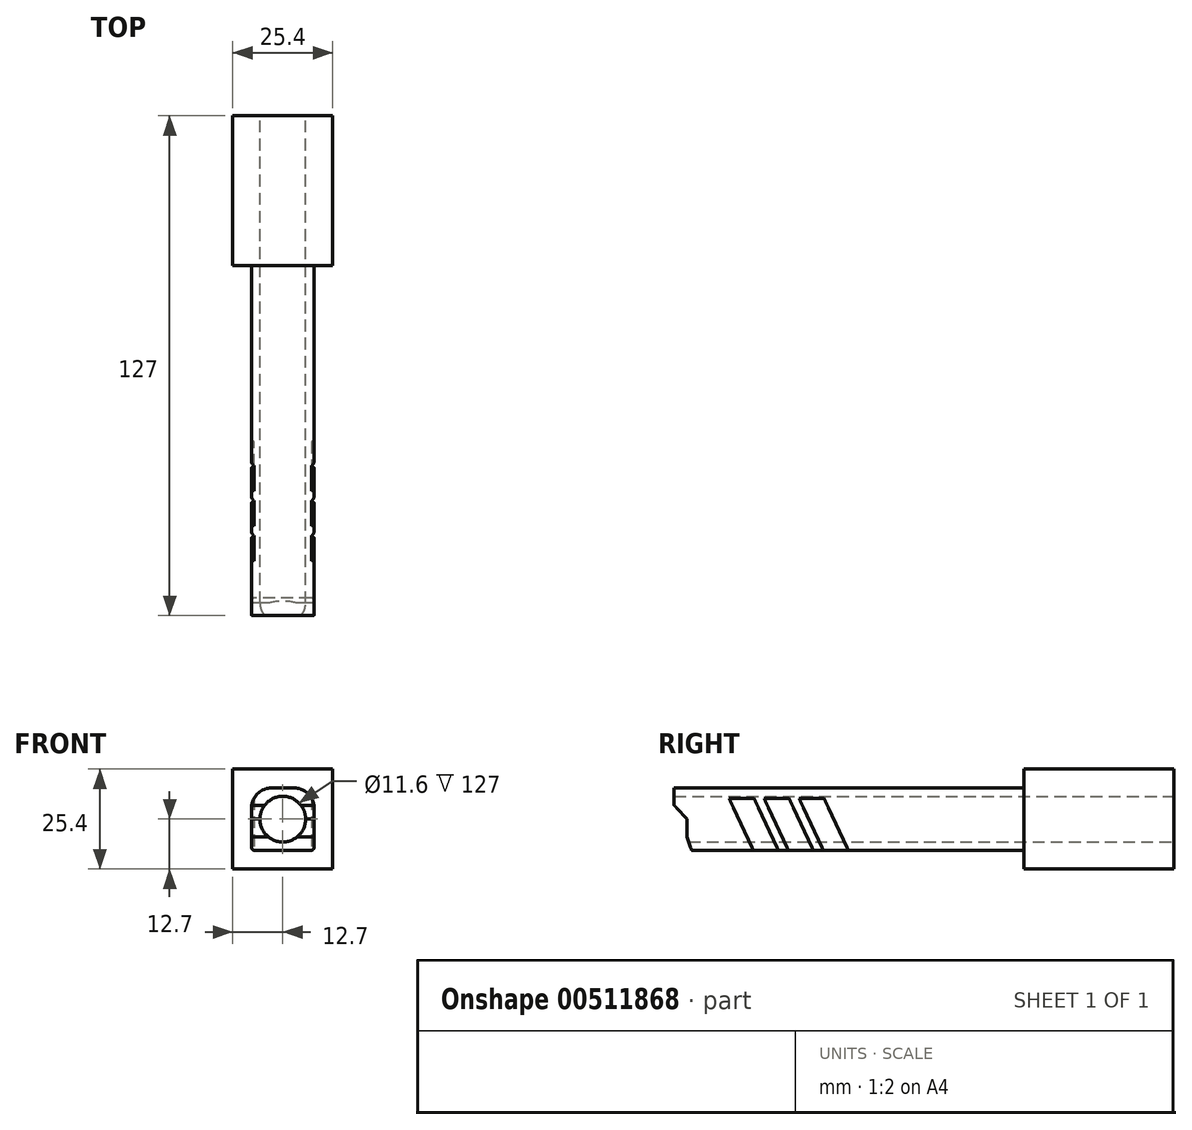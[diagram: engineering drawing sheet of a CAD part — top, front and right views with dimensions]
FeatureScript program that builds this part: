
annotation { "Feature Type Name" : "Feature", "Feature Type Description" : "" }
export const myFeature = defineFeature(function(context is Context, id is Id, definition is map)
    precondition{}
    {
        {
            var Q0;
            Q0=qCreatedBy(makeId("Front.planeOp"),FACE);
            var sketch = newSketch(context, id + "F0", { "sketchPlane" : qUnion([Q0])});
            skLineSegment(sketch, "E0.bottom", {"start": v(12.7, -12.7) * mm, "end": v(-12.7, -12.7) * mm});
            skLineSegment(sketch, "E0.top", {"start": v(12.7, 12.7) * mm, "end": v(-12.7, 12.7) * mm});
            skLineSegment(sketch, "E0.left", {"start": v(12.7, -12.7) * mm, "end": v(12.7, 12.7) * mm});
            skLineSegment(sketch, "E0.right", {"start": v(-12.7, -12.7) * mm, "end": v(-12.7, 12.7) * mm});
            skPoint(sketch, "E0.middle", {"position": v(0, 0) * mm});
            skCircle(sketch, "E1", {"center": v(0, 0) * mm, "radius": 7.94 * mm});
            skCircle(sketch, "E2", {"center": v(0, 0) * mm, "radius": 5.8 * mm});
            skLineSegment(sketch, "E3.bottom", {"start": v(-7.94, -7.94) * mm, "end": v(7.94, -7.94) * mm});
            skLineSegment(sketch, "E3.top", {"start": v(-7.94, 7.94) * mm, "end": v(7.94, 7.94) * mm});
            skLineSegment(sketch, "E3.left", {"start": v(-7.94, -7.94) * mm, "end": v(-7.94, 7.94) * mm});
            skLineSegment(sketch, "E3.right", {"start": v(7.94, -7.94) * mm, "end": v(7.94, 7.94) * mm});
            skSolve(sketch);
        }
        {
            var Q0;
            Q0=qSketchRegion(id+"F0",true);
            var Q1;
            Q1=makeQuery(id+"F0.imprint","IMPRINT",FACE,{"disambiguationData":[TD([[makeQuery(id+"F0.imprint","IMPRINT",EDGE,{"derivedFrom":sQuery(id+"F0.wireOp",EDGE,"E1")}),1.0]])]});
            extrude(context, id + "F1", {"entities" : qUnion([Q0, Q1]), "depth" : 38.1 * mm});
        }
        {
            var Q0;
            Q0=makeQuery(id+"F0.imprint","IMPRINT",FACE,{"disambiguationData":[TD([[makeQuery(id+"F0.imprint","IMPRINT",EDGE,{"derivedFrom":sQuery(id+"F0.wireOp",EDGE,"E1")}),1.0]])]});
            extrude(context, id + "F2", {"entities" : qUnion([Q0]), "operationType" : NewBodyOperationType.ADD, "depth" : 127 * mm, "offsetDistance" : 25.4 * mm});
        }
        {
            var Q0;
            {var subQ0=sQuery(id+"F0.wireOp",EDGE,"E3.right");var subQ1=sQuery(id+"F0.wireOp",EDGE,"E1");var subQ2=makeQuery(id+"F0.imprint","INTERSECT",VERTEX,{"derivedFrom":[subQ1,subQ0]});Q0=makeQuery(id+"F0.imprint","IMPRINT",FACE,{"disambiguationData":[TD([[makeQuery(id+"F0.imprint","IMPRINT",EDGE,{"disambiguationData":[TD([[subQ2,1.0]])],"derivedFrom":subQ1}),-1.0]])]});}
            var Q1;
            {var subQ0=sQuery(id+"F0.wireOp",EDGE,"E3.top");var subQ1=sQuery(id+"F0.wireOp",EDGE,"E1");var subQ2=makeQuery(id+"F0.imprint","INTERSECT",VERTEX,{"derivedFrom":[subQ1,subQ0]});Q1=makeQuery(id+"F0.imprint","IMPRINT",FACE,{"disambiguationData":[TD([[makeQuery(id+"F0.imprint","IMPRINT",EDGE,{"disambiguationData":[TD([[subQ2,1.0]])],"derivedFrom":subQ1}),-1.0]])]});}
            var Q2;
            {var subQ0=sQuery(id+"F0.wireOp",EDGE,"E3.top");var subQ1=sQuery(id+"F0.wireOp",EDGE,"E1");var subQ2=makeQuery(id+"F0.imprint","INTERSECT",VERTEX,{"derivedFrom":[subQ1,subQ0]});Q2=makeQuery(id+"F0.imprint","IMPRINT",FACE,{"disambiguationData":[TD([[makeQuery(id+"F0.imprint","IMPRINT",EDGE,{"disambiguationData":[TD([[subQ2,-1.0]])],"derivedFrom":subQ1}),-1.0]])]});}
            var Q3;
            {var subQ0=sQuery(id+"F0.wireOp",EDGE,"E3.left");var subQ1=sQuery(id+"F0.wireOp",EDGE,"E1");var subQ2=makeQuery(id+"F0.imprint","INTERSECT",VERTEX,{"derivedFrom":[subQ1,subQ0]});Q3=makeQuery(id+"F0.imprint","IMPRINT",FACE,{"disambiguationData":[TD([[makeQuery(id+"F0.imprint","IMPRINT",EDGE,{"disambiguationData":[TD([[subQ2,-1.0]])],"derivedFrom":subQ1}),-1.0]])]});}
            extrude(context, id + "F3", {"entities" : qUnion([Q0, Q1, Q2, Q3]), "operationType" : NewBodyOperationType.ADD, "depth" : 127 * mm, "offsetDistance" : 25.4 * mm});
        }
        {
            var Q0;
            {var subQ0=sQuery(id+"F0.wireOp",EDGE,"E3.left");Q0=makeQuery(id+"F3.boolean.opBoolean","MERGE",FACE,{"derivedFrom":[makeQuery(id+"F3.opExtrude","SWEPT_FACE",FACE,{"disambiguationData":[OSD([subQ0]),TDD([makeQuery(id+"F0.imprint","IMPRINT",EDGE,{"disambiguationData":[TD([[makeQuery(id+"F0.imprint","INTERSECT",VERTEX,{"derivedFrom":[sQuery(id+"F0.wireOp",EDGE,"E3.bottom"),subQ0]}),-1.0]])],"derivedFrom":subQ0})])]}),makeQuery(id+"F3.opExtrude","SWEPT_FACE",FACE,{"disambiguationData":[OSD([subQ0]),TDD([makeQuery(id+"F0.imprint","IMPRINT",EDGE,{"disambiguationData":[TD([[makeQuery(id+"F0.imprint","INTERSECT",VERTEX,{"derivedFrom":[sQuery(id+"F0.wireOp",EDGE,"E3.top"),subQ0]}),1.0]])],"derivedFrom":subQ0})])]})]});}
            var sketch = newSketch(context, id + "F4", { "sketchPlane" : qUnion([Q0])});
            skLineSegment(sketch, "E4", {"start": v(127, 7.94) * mm, "end": v(114.3, 7.94) * mm});
            skLineSegment(sketch, "E5", {"start": v(114.3, 7.94) * mm, "end": v(106.9, -7.94) * mm});
            skLineSegment(sketch, "E6", {"start": v(114.3, 7.94) * mm, "end": v(107.95, 7.94) * mm});
            skLineSegment(sketch, "E7", {"start": v(107.95, 7.94) * mm, "end": v(100.55, -7.94) * mm});
            skLineSegment(sketch, "E8", {"start": v(100.55, -7.94) * mm, "end": v(106.9, -7.94) * mm});
            skLineSegment(sketch, "E9", {"start": v(105.4, 7.94) * mm, "end": v(98, -7.94) * mm});
            skLineSegment(sketch, "E10", {"start": v(105.4, 7.94) * mm, "end": v(99.06, 7.94) * mm});
            skLineSegment(sketch, "E11", {"start": v(99.06, 7.94) * mm, "end": v(91.66, -7.94) * mm});
            skLineSegment(sketch, "E12", {"start": v(91.66, -7.94) * mm, "end": v(98, -7.94) * mm});
            skLineSegment(sketch, "E13", {"start": v(96.52, 7.94) * mm, "end": v(89.12, -7.94) * mm});
            skLineSegment(sketch, "E14", {"start": v(96.52, 7.94) * mm, "end": v(90.17, 7.94) * mm});
            skLineSegment(sketch, "E15", {"start": v(90.17, 7.94) * mm, "end": v(82.77, -7.94) * mm});
            skLineSegment(sketch, "E16", {"start": v(82.77, -7.94) * mm, "end": v(89.12, -7.94) * mm});
            skSolve(sketch);
        }
        {
            var Q0;
            Q0=qSketchRegion(id+"F4",true);
            extrude(context, id + "F5", {"entities" : qUnion([Q0]), "operationType" : NewBodyOperationType.REMOVE, "oppositeDirection" : true, "depth" : 0.64 * mm, "offsetDistance" : 25.4 * mm});
        }
        {
            var Q0;
            {var subQ0=sQuery(id+"F0.wireOp",EDGE,"E3.right");Q0=makeQuery(id+"F3.boolean.opBoolean","MERGE",FACE,{"derivedFrom":[makeQuery(id+"F3.opExtrude","SWEPT_FACE",FACE,{"disambiguationData":[OSD([subQ0]),TDD([makeQuery(id+"F0.imprint","IMPRINT",EDGE,{"disambiguationData":[TD([[makeQuery(id+"F0.imprint","INTERSECT",VERTEX,{"derivedFrom":[sQuery(id+"F0.wireOp",EDGE,"E3.bottom"),subQ0]}),-1.0]])],"derivedFrom":subQ0})])]}),makeQuery(id+"F3.opExtrude","SWEPT_FACE",FACE,{"disambiguationData":[OSD([subQ0]),TDD([makeQuery(id+"F0.imprint","IMPRINT",EDGE,{"disambiguationData":[TD([[makeQuery(id+"F0.imprint","INTERSECT",VERTEX,{"derivedFrom":[sQuery(id+"F0.wireOp",EDGE,"E3.top"),subQ0]}),1.0]])],"derivedFrom":subQ0})])]})]});}
            var sketch = newSketch(context, id + "F6", { "sketchPlane" : qUnion([Q0])});
            skLineSegment(sketch, "E17", {"start": v(-127, 7.94) * mm, "end": v(-114.3, 7.94) * mm});
            skLineSegment(sketch, "E18", {"start": v(-114.3, 7.94) * mm, "end": v(-106.9, -7.94) * mm});
            skLineSegment(sketch, "E19", {"start": v(-106.9, -7.94) * mm, "end": v(-100.55, -7.94) * mm});
            skLineSegment(sketch, "E20", {"start": v(-100.55, -7.94) * mm, "end": v(-107.95, 7.94) * mm});
            skLineSegment(sketch, "E21", {"start": v(-107.95, 7.94) * mm, "end": v(-114.3, 7.94) * mm});
            skLineSegment(sketch, "E22", {"start": v(-105.41, 7.94) * mm, "end": v(-98, -7.94) * mm});
            skLineSegment(sketch, "E23", {"start": v(-98, -7.94) * mm, "end": v(-91.66, -7.94) * mm});
            skLineSegment(sketch, "E24", {"start": v(-91.66, -7.94) * mm, "end": v(-99.06, 7.94) * mm});
            skLineSegment(sketch, "E25", {"start": v(-99.06, 7.94) * mm, "end": v(-105.4, 7.94) * mm});
            skLineSegment(sketch, "E26", {"start": v(-96.52, 7.94) * mm, "end": v(-89.12, -7.94) * mm});
            skLineSegment(sketch, "E27", {"start": v(-89.12, -7.94) * mm, "end": v(-82.77, -7.94) * mm});
            skLineSegment(sketch, "E28", {"start": v(-82.77, -7.94) * mm, "end": v(-90.17, 7.94) * mm});
            skLineSegment(sketch, "E29", {"start": v(-90.17, 7.94) * mm, "end": v(-96.52, 7.94) * mm});
            skSolve(sketch);
        }
        {
            var Q0;
            Q0=qSketchRegion(id+"F6",true);
            extrude(context, id + "F7", {"entities" : qUnion([Q0]), "operationType" : NewBodyOperationType.REMOVE, "oppositeDirection" : true, "depth" : 0.64 * mm, "offsetDistance" : 25.4 * mm});
        }
        {
            var Q0;
            {var subQ0=sQuery(id+"F0.wireOp",EDGE,"E3.right");var subQ1=sQuery(id+"F0.wireOp",EDGE,"E3.top");Q0=makeQuery(id+"F7.boolean.opBoolean","SPLIT",EDGE,{"disambiguationData":[TD([makeQuery(id+"F7.opExtrude","SWEPT_FACE",FACE,{"disambiguationData":[OSD([sQuery(id+"F6.wireOp",EDGE,"E28")])]})])],"derivedFrom":makeQuery(id+"F3.opExtrude","SWEPT_EDGE",EDGE,{"disambiguationData":[OSD([subQ1,subQ0])]})});}
            var Q1;
            {var subQ0=sQuery(id+"F0.wireOp",EDGE,"E3.left");var subQ3=sQuery(id+"F0.wireOp",EDGE,"E3.top");Q1=makeQuery(id+"F5.boolean.opBoolean","SPLIT",EDGE,{"disambiguationData":[TD([makeQuery(id+"F5.opExtrude","SWEPT_FACE",FACE,{"disambiguationData":[OSD([sQuery(id+"F4.wireOp",EDGE,"E5")])]})])],"derivedFrom":makeQuery(id+"F3.opExtrude","SWEPT_EDGE",EDGE,{"disambiguationData":[OSD([subQ3,subQ0])]})});}
            fillet(context, id + "F8", {"entities" : qUnion([Q0, Q1]), "radius" : 5.08 * mm, "tangentPropagation" : true, "allowEdgeOverflow" : false});
        }
        {
            var Q0;
            {var subQ0=sQuery(id+"F0.wireOp",EDGE,"E3.left");var subQ1=sQuery(id+"F0.wireOp",EDGE,"E3.bottom");Q0=makeQuery(id+"F5.boolean.opBoolean","SPLIT",EDGE,{"disambiguationData":[TD([makeQuery(id+"F5.opExtrude","SWEPT_FACE",FACE,{"disambiguationData":[OSD([sQuery(id+"F4.wireOp",EDGE,"E5")])]})])],"derivedFrom":makeQuery(id+"F3.opExtrude","SWEPT_EDGE",EDGE,{"disambiguationData":[OSD([subQ1,subQ0])]})});}
            var Q1;
            {var subQ1=sQuery(id+"F0.wireOp",EDGE,"E3.bottom");var subQ3=sQuery(id+"F0.wireOp",EDGE,"E3.right");Q1=makeQuery(id+"F7.boolean.opBoolean","SPLIT",EDGE,{"disambiguationData":[TD([makeQuery(id+"F7.opExtrude","SWEPT_FACE",FACE,{"disambiguationData":[OSD([sQuery(id+"F6.wireOp",EDGE,"E18")])]})])],"derivedFrom":makeQuery(id+"F3.opExtrude","SWEPT_EDGE",EDGE,{"disambiguationData":[OSD([subQ1,subQ3])]})});}
            fillet(context, id + "F9", {"entities" : qUnion([Q0, Q1]), "radius" : 0.76 * mm, "tangentPropagation" : true, "allowEdgeOverflow" : false});
        }
        {
            var Q0;
            {var subQ0=sQuery(id+"F0.wireOp",EDGE,"E3.left");var subQ1=sQuery(id+"F0.wireOp",EDGE,"E3.bottom");var subQ3=sQuery(id+"F0.wireOp",EDGE,"E3.top");var subQ6=makeQuery(id+"F0.imprint","INTERSECT",VERTEX,{"derivedFrom":[subQ1,subQ0]});var subQ7=makeQuery(id+"F0.imprint","INTERSECT",VERTEX,{"derivedFrom":[subQ3,subQ0]});Q0=makeQuery(id+"F5.boolean.opBoolean","SPLIT",FACE,{"disambiguationData":[TD([makeQuery(id+"F5.opExtrude","SWEPT_FACE",FACE,{"disambiguationData":[OSD([sQuery(id+"F4.wireOp",EDGE,"E5")])]})])],"derivedFrom":makeQuery(id+"F3.boolean.opBoolean","MERGE",FACE,{"derivedFrom":[makeQuery(id+"F3.opExtrude","SWEPT_FACE",FACE,{"disambiguationData":[OSD([subQ0]),TDD([makeQuery(id+"F0.imprint","IMPRINT",EDGE,{"disambiguationData":[TD([[subQ6,-1.0]])],"derivedFrom":subQ0})])]}),makeQuery(id+"F3.opExtrude","SWEPT_FACE",FACE,{"disambiguationData":[OSD([subQ0]),TDD([makeQuery(id+"F0.imprint","IMPRINT",EDGE,{"disambiguationData":[TD([[subQ7,1.0]])],"derivedFrom":subQ0})])]})]})});}
            var sketch = newSketch(context, id + "F10", { "sketchPlane" : qUnion([Q0])});
            skLineSegment(sketch, "E30", {"start": v(129.12, 15.12) * mm, "end": v(139.4, 2.86) * mm});
            skLineSegment(sketch, "E31", {"start": v(139.4, 2.86) * mm, "end": v(129.65, -9.53) * mm});
            skLineSegment(sketch, "E32", {"start": v(129.65, -9.53) * mm, "end": v(129.12, 15.12) * mm});
            skSolve(sketch);
        }
        {
            var Q0;
            Q0 = qSketchRegion(id + "F10", true);
            extrude(context, id + "F11", {"entities" : qUnion([Q0]), "operationType" : NewBodyOperationType.REMOVE, "oppositeDirection" : true, "depth" : 25.4 * mm, "offsetDistance" : 25.4 * mm});
        }
        {
            var Q0;
            {var subQ0=sQuery(id+"F0.wireOp",EDGE,"E3.left");var subQ1=sQuery(id+"F0.wireOp",EDGE,"E3.bottom");var subQ3=sQuery(id+"F0.wireOp",EDGE,"E3.top");var subQ6=makeQuery(id+"F0.imprint","INTERSECT",VERTEX,{"derivedFrom":[subQ1,subQ0]});var subQ7=makeQuery(id+"F0.imprint","INTERSECT",VERTEX,{"derivedFrom":[subQ3,subQ0]});Q0=makeQuery(id+"F5.boolean.opBoolean","SPLIT",FACE,{"disambiguationData":[TD([makeQuery(id+"F5.opExtrude","SWEPT_FACE",FACE,{"disambiguationData":[OSD([sQuery(id+"F4.wireOp",EDGE,"E5")])]})])],"derivedFrom":makeQuery(id+"F3.boolean.opBoolean","MERGE",FACE,{"derivedFrom":[makeQuery(id+"F3.opExtrude","SWEPT_FACE",FACE,{"disambiguationData":[OSD([subQ0]),TDD([makeQuery(id+"F0.imprint","IMPRINT",EDGE,{"disambiguationData":[TD([[subQ6,-1.0]])],"derivedFrom":subQ0})])]}),makeQuery(id+"F3.opExtrude","SWEPT_FACE",FACE,{"disambiguationData":[OSD([subQ0]),TDD([makeQuery(id+"F0.imprint","IMPRINT",EDGE,{"disambiguationData":[TD([[subQ7,1.0]])],"derivedFrom":subQ0})])]})]})});}
            var sketch = newSketch(context, id + "F12", { "sketchPlane" : qUnion([Q0])});
            skLineSegment(sketch, "E33", {"start": v(131.5, 8.46) * mm, "end": v(123.8, 0) * mm});
            skLineSegment(sketch, "E34", {"start": v(123.8, 0) * mm, "end": v(123.8, -4.51) * mm});
            skLineSegment(sketch, "E35", {"start": v(123.8, -4.51) * mm, "end": v(121.05, -12.1) * mm});
            skLineSegment(sketch, "E36", {"start": v(131.5, 8.46) * mm, "end": v(131.5, -9.18) * mm});
            skLineSegment(sketch, "E37", {"start": v(131.5, -9.18) * mm, "end": v(121.05, -12.1) * mm});
            skSolve(sketch);
        }
        {
            var Q0;
            Q0 = qSketchRegion(id + "F12", true);
            extrude(context, id + "F13", {"entities" : qUnion([Q0]), "operationType" : NewBodyOperationType.REMOVE, "oppositeDirection" : true, "depth" : 25.4 * mm, "offsetDistance" : 25.4 * mm});
        }
    });
